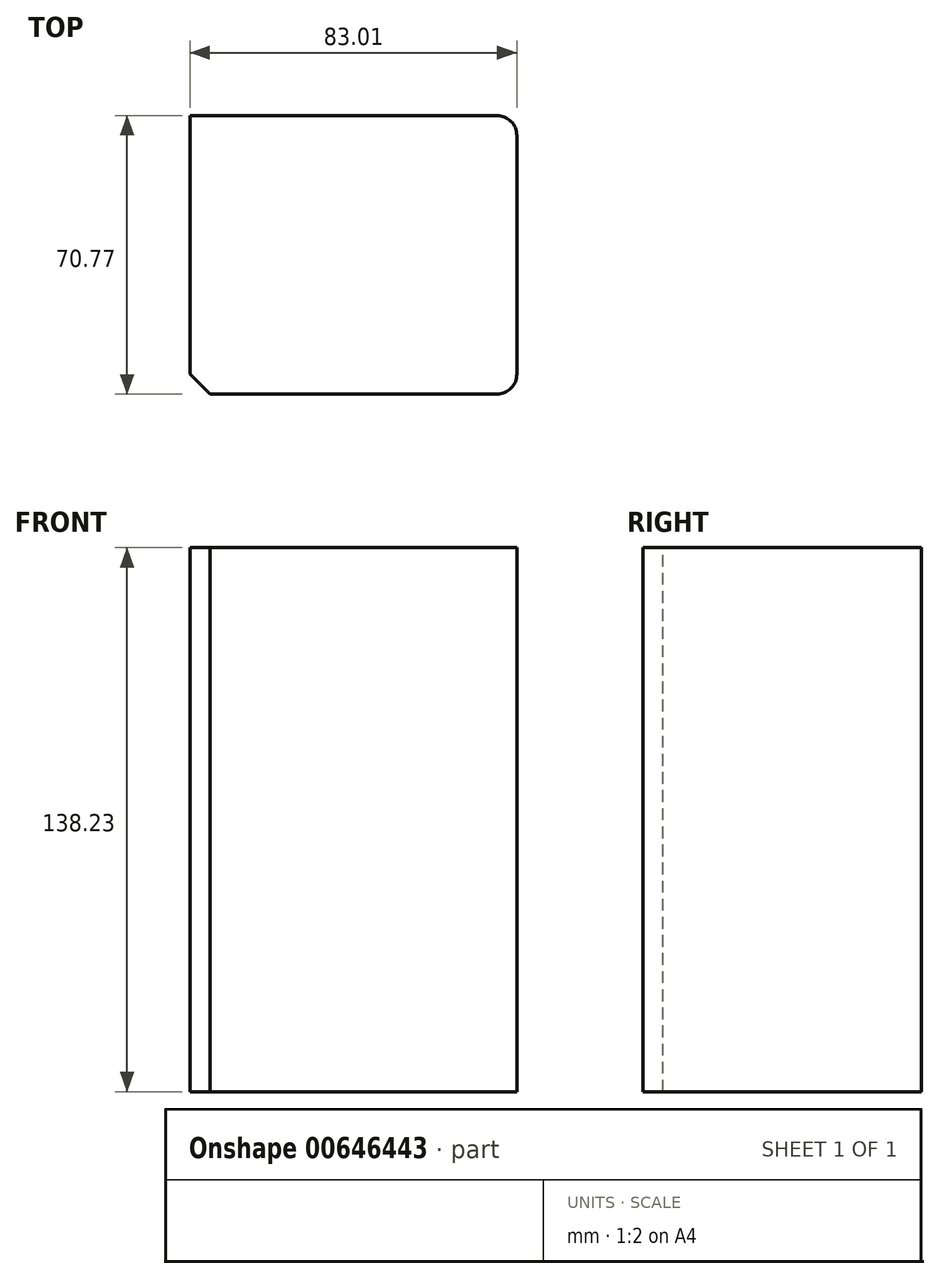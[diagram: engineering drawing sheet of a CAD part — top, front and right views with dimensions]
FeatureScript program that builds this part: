
annotation { "Feature Type Name" : "Feature", "Feature Type Description" : "" }
export const myFeature = defineFeature(function(context is Context, id is Id, definition is map)
    precondition{}
    {
        {
            var Q0;
            Q0=qCreatedBy(makeId("Top.planeOp"),FACE);
            var sketch = newSketch(context, id + "F0", { "sketchPlane" : qUnion([Q0])});
            skLineSegment(sketch, "E0.bottom", {"start": v(-40.09, -42.97) * mm, "end": v(42.92, -42.97) * mm});
            skLineSegment(sketch, "E0.top", {"start": v(-40.09, 27.8) * mm, "end": v(42.92, 27.8) * mm});
            skLineSegment(sketch, "E0.left", {"start": v(-40.09, -42.97) * mm, "end": v(-40.09, 27.8) * mm});
            skLineSegment(sketch, "E0.right", {"start": v(42.92, -42.97) * mm, "end": v(42.92, 27.8) * mm});
            skSolve(sketch);
        }
        {
            var Q0;
            Q0 = qSketchRegion(id + "F0", true);
            var Q1;
            Q1=makeQuery(id+"F0.imprint","IMPRINT",FACE,{"disambiguationData":[TD([[makeQuery(id+"F0.imprint","IMPRINT",EDGE,{"derivedFrom":sQuery(id+"F0.wireOp",EDGE,"E0.bottom")}),1.0]])]});
            extrude(context, id + "F1", {"entities" : qUnion([Q0, Q1]), "depth" : 25.4 * mm, "offsetDistance" : 25.4 * mm});
        }
        {
            var Q0;
            Q0=makeQuery(id+"F1.opExtrude","CAP_FACE",FACE,{"disambiguationData":[OSD([sQuery(id+"F0.wireOp",EDGE,"E0.bottom"),sQuery(id+"F0.wireOp",EDGE,"E0.top"),sQuery(id+"F0.wireOp",EDGE,"E0.left"),sQuery(id+"F0.wireOp",EDGE,"E0.right")])],"isStart":false});
            var sketch = newSketch(context, id + "F2", { "sketchPlane" : qUnion([Q0])});
            skSolve(sketch);
        }
        {
            var Q0;
            Q0=makeQuery(id+"F2.imprint","IMPRINT",FACE,{"disambiguationData":[TD([[makeQuery(id+"F2.imprint","IMPRINT",EDGE,{"derivedFrom":makeQuery(id+"F1.opExtrude","CAP_EDGE",EDGE,{"disambiguationData":[OSD([sQuery(id+"F0.wireOp",EDGE,"E0.bottom")])],"isStart":false})}),1.0]])]});
            extrude(context, id + "F3", {"entities" : qUnion([Q0]), "operationType" : NewBodyOperationType.ADD, "depth" : 112.83 * mm, "offsetDistance" : 25.4 * mm});
        }
        {
            var Q0;
            {var subQ0=sQuery(id+"F0.wireOp",EDGE,"E0.right");var subQ1=sQuery(id+"F0.wireOp",EDGE,"E0.bottom");Q0=makeQuery(id+"F3.boolean.opBoolean","MERGE",EDGE,{"derivedFrom":[makeQuery(id+"F1.opExtrude","SWEPT_EDGE",EDGE,{"disambiguationData":[OSD([subQ1,subQ0])]}),makeQuery(id+"F3.opExtrude","SWEPT_EDGE",EDGE,{"disambiguationData":[OSD([subQ1,subQ0])]})]});}
            var Q1;
            {var subQ0=sQuery(id+"F0.wireOp",EDGE,"E0.right");var subQ1=sQuery(id+"F0.wireOp",EDGE,"E0.top");Q1=makeQuery(id+"F3.boolean.opBoolean","MERGE",EDGE,{"derivedFrom":[makeQuery(id+"F1.opExtrude","SWEPT_EDGE",EDGE,{"disambiguationData":[OSD([subQ1,subQ0])]}),makeQuery(id+"F3.opExtrude","SWEPT_EDGE",EDGE,{"disambiguationData":[OSD([subQ1,subQ0])]})]});}
            fillet(context, id + "F4", {"entities" : qUnion([Q0, Q1]), "radius" : 5.08 * mm, "tangentPropagation" : true, "allowEdgeOverflow" : false});
        }
        {
            var Q0;
            {var subQ0=sQuery(id+"F0.wireOp",EDGE,"E0.left");var subQ1=sQuery(id+"F0.wireOp",EDGE,"E0.bottom");Q0=makeQuery(id+"F3.boolean.opBoolean","MERGE",EDGE,{"derivedFrom":[makeQuery(id+"F1.opExtrude","SWEPT_EDGE",EDGE,{"disambiguationData":[OSD([subQ1,subQ0])]}),makeQuery(id+"F3.opExtrude","SWEPT_EDGE",EDGE,{"disambiguationData":[OSD([subQ1,subQ0])]})]});}
            chamfer(context, id + "F5", {"entities" : qUnion([Q0]), "width" : 5.08 * mm, "tangentPropagation" : true});
        }
    });
